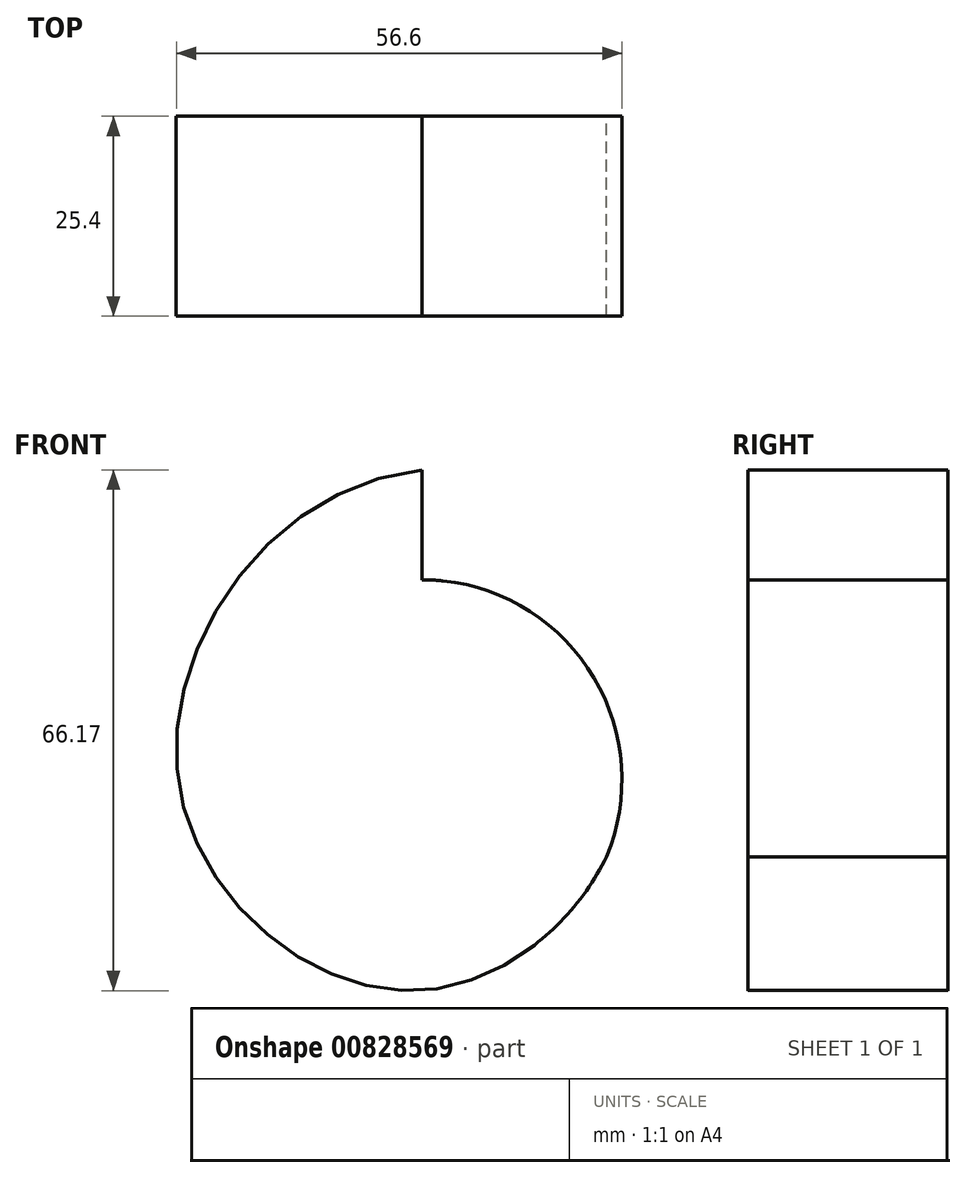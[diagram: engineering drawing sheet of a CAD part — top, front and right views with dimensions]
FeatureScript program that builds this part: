
annotation { "Feature Type Name" : "Feature", "Feature Type Description" : "" }
export const myFeature = defineFeature(function(context is Context, id is Id, definition is map)
    precondition{}
    {
        {
            var Q0;
            Q0=qCreatedBy(makeId("Front.planeOp"),FACE);
            var sketch = newSketch(context, id + "F0", { "sketchPlane" : qUnion([Q0])});
            skCircle(sketch, "E0", {"center": v(0, 0) * mm, "radius": 25.4 * mm});
            skLineSegment(sketch, "E1", {"start": v(0, 25.4) * mm, "end": v(0, 39.37) * mm});
            skLineSegment(sketch, "E2", {"start": v(0, 0) * mm, "end": v(0, 25.4) * mm, "construction": true});
            skFitSpline(sketch, "E3", {"points": [v(0, 39.37) * mm, v(-30.96, 0) * mm, v(0, -26.75) * mm, v(26.06, 0) * mm, v(0, 25.4) * mm], "startDerivative": vector(-212.33, -22.1) * mm, "endDerivative": vector(-204.7, 1.82) * mm});
            skSolve(sketch);
        }
        {
            var Q0;
            {var subQ1=sQuery(id+"F0.wireOp",EDGE,"E1");Q0=makeQuery(id+"F0.imprint","IMPRINT",FACE,{"disambiguationData":[TD([[makeQuery(id+"F0.imprint","IMPRINT",EDGE,{"derivedFrom":subQ1}),1.0]])]});}
            var Q1;
            {var subQ0=sQuery(id+"F0.wireOp",EDGE,"E3");var subQ1=sQuery(id+"F0.wireOp",EDGE,"E0");var subQ3=makeQuery(id+"F0.imprint","INTERSECT",VERTEX,{"derivedFrom":[subQ1,subQ0]});Q1=makeQuery(id+"F0.imprint","IMPRINT",FACE,{"disambiguationData":[TD([[makeQuery(id+"F0.imprint","IMPRINT",EDGE,{"disambiguationData":[TD([[subQ3,1.0]])],"derivedFrom":subQ1}),1.0]])]});}
            extrude(context, id + "F1", {"entities" : qUnion([Q0, Q1]), "depth" : 25.4 * mm, "offsetDistance" : 25.4 * mm});
        }
    });
